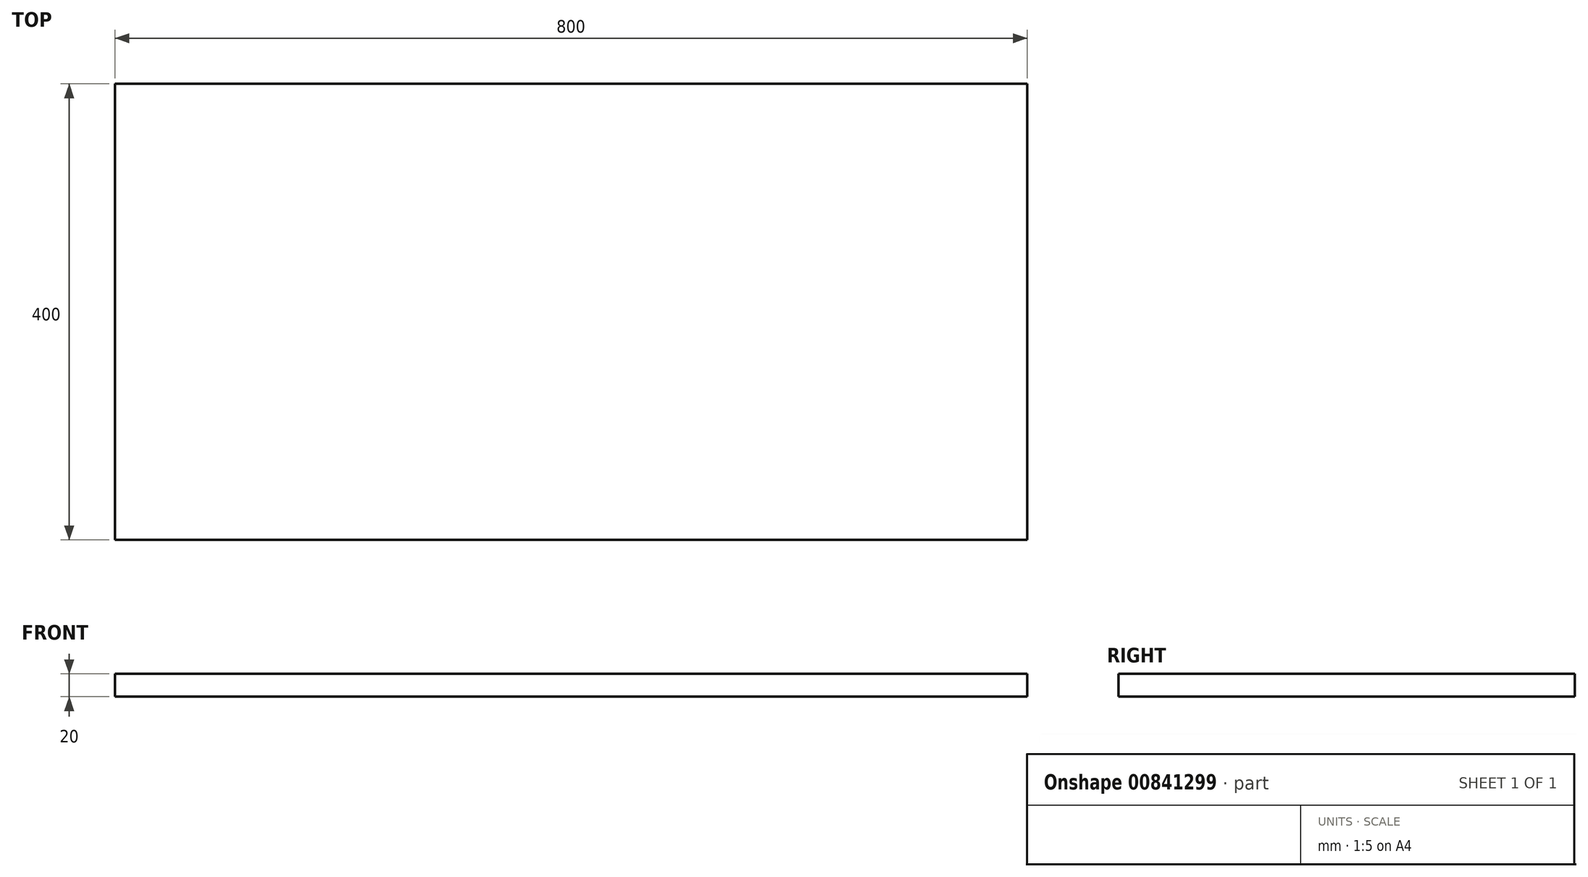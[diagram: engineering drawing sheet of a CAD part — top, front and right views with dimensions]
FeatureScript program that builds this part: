
annotation { "Feature Type Name" : "Feature", "Feature Type Description" : "" }
export const myFeature = defineFeature(function(context is Context, id is Id, definition is map)
    precondition{}
    {
        {
            var Q0;
            Q0=qCreatedBy(makeId("Top.planeOp"),FACE);
            var sketch = newSketch(context, id + "F0", { "sketchPlane" : qUnion([Q0])});
            skLineSegment(sketch, "E0.bottom", {"start": v(-400, 200) * mm, "end": v(400, 200) * mm});
            skLineSegment(sketch, "E0.top", {"start": v(-400, -200) * mm, "end": v(400, -200) * mm});
            skLineSegment(sketch, "E0.left", {"start": v(-400, 200) * mm, "end": v(-400, -200) * mm});
            skLineSegment(sketch, "E0.right", {"start": v(400, 200) * mm, "end": v(400, -200) * mm});
            skPoint(sketch, "E0.middle", {"position": v(0, 0) * mm});
            skPoint(sketch, "E1.visualSharp", {"position": v(-400, 200) * mm});
            skPoint(sketch, "E2.visualSharp", {"position": v(-400, -200) * mm});
            skPoint(sketch, "E3.visualSharp", {"position": v(400, -200) * mm});
            skPoint(sketch, "E4.visualSharp", {"position": v(400, 200) * mm});
            skSolve(sketch);
        }
        {
            var Q0;
            Q0=makeQuery(id+"F0.imprint","IMPRINT",FACE,{"disambiguationData":[TD([[makeQuery(id+"F0.imprint","IMPRINT",EDGE,{"derivedFrom":sQuery(id+"F0.wireOp",EDGE,"E0.bottom")}),-1.0]])]});
            extrude(context, id + "F1", {"entities" : qUnion([Q0]), "depth" : 20 * mm, "offsetDistance" : 25 * mm});
        }
    });
